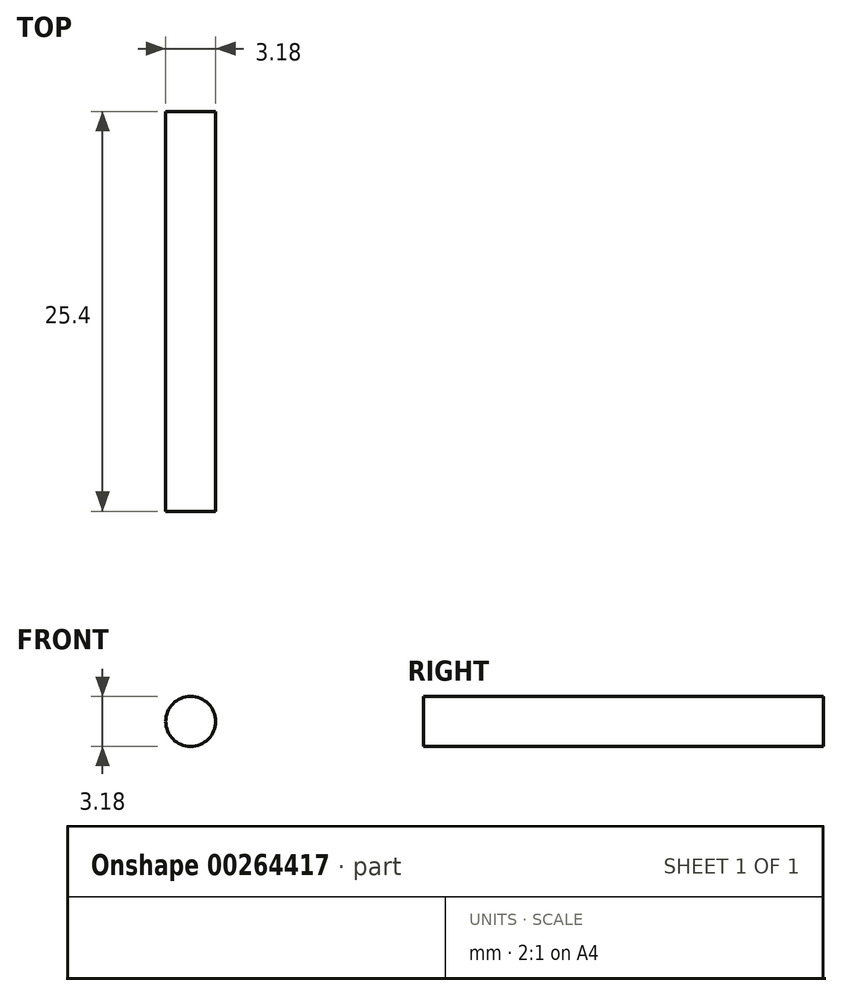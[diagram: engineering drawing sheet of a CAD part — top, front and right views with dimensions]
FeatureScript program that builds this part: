
annotation { "Feature Type Name" : "Feature", "Feature Type Description" : "" }
export const myFeature = defineFeature(function(context is Context, id is Id, definition is map)
    precondition{}
    {
        {
            var Q0;
            Q0=qCreatedBy(makeId("Front.planeOp"),FACE);
            var sketch = newSketch(context, id + "F0", { "sketchPlane" : qUnion([Q0])});
            skCircle(sketch, "E0", {"center": v(0, 0) * mm, "radius": 1.59 * mm});
            skSolve(sketch);
        }
        {
            var Q0;
            Q0=qSketchRegion(id+"F0",true);
            extrude(context, id + "F1", {"entities" : qUnion([Q0]), "depth" : 25.4 * mm});
        }
    });
